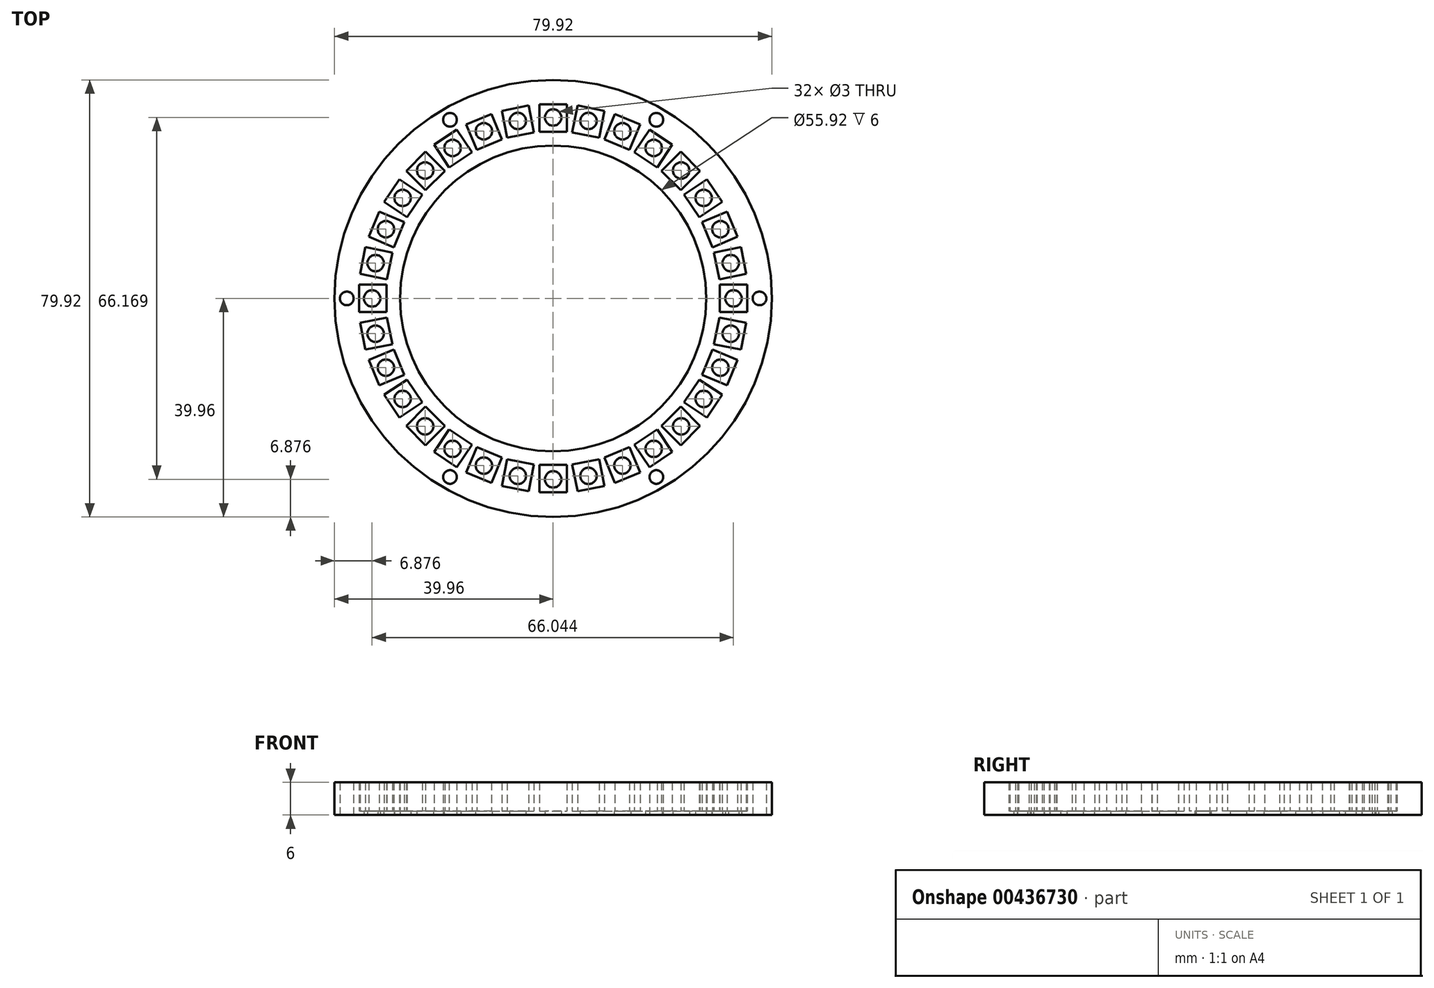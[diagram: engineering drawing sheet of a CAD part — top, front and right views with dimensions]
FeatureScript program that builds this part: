
annotation { "Feature Type Name" : "Feature", "Feature Type Description" : "" }
export const myFeature = defineFeature(function(context is Context, id is Id, definition is map)
    precondition{}
    {
        {
            var Q0;
            Q0=qCreatedBy(makeId("Top.planeOp"),FACE);
            var sketch = newSketch(context, id + "F0", { "sketchPlane" : qUnion([Q0])});
            skPoint(sketch, "E0.0.midPoint", {"position": v(30.46, 0) * mm});
            skLineSegment(sketch, "E1", {"start": v(0, 0) * mm, "end": v(46.47, 0) * mm, "construction": true});
            skLineSegment(sketch, "E2", {"start": v(30.46, 2.5) * mm, "end": v(35.46, 2.5) * mm, "construction": true});
            skLineSegment(sketch, "E3", {"start": v(35.46, 2.5) * mm, "end": v(35.46, -2.5) * mm, "construction": true});
            skLineSegment(sketch, "E4", {"start": v(35.46, -2.5) * mm, "end": v(30.46, -2.5) * mm, "construction": true});
            skCircle(sketch, "E5.cCircle", {"center": v(0, 0) * mm, "radius": 30.46 * mm, "construction": true});
            skLineSegment(sketch, "E5.0", {"start": v(30.46, 3) * mm, "end": v(30.46, -3) * mm});
            skLineSegment(sketch, "E5.1", {"start": v(30.46, -3) * mm, "end": v(29.29, -8.88) * mm});
            skLineSegment(sketch, "E5.2", {"start": v(29.29, -8.88) * mm, "end": v(27, -14.43) * mm});
            skLineSegment(sketch, "E5.3", {"start": v(27, -14.43) * mm, "end": v(23.66, -19.42) * mm});
            skLineSegment(sketch, "E5.4", {"start": v(23.66, -19.42) * mm, "end": v(19.42, -23.66) * mm});
            skLineSegment(sketch, "E5.5", {"start": v(19.42, -23.66) * mm, "end": v(14.43, -27) * mm});
            skLineSegment(sketch, "E5.6", {"start": v(14.43, -27) * mm, "end": v(8.88, -29.29) * mm});
            skLineSegment(sketch, "E5.7", {"start": v(8.88, -29.29) * mm, "end": v(3, -30.46) * mm});
            skLineSegment(sketch, "E5.8", {"start": v(3, -30.46) * mm, "end": v(-3, -30.46) * mm});
            skLineSegment(sketch, "E5.9", {"start": v(-3, -30.46) * mm, "end": v(-8.88, -29.29) * mm});
            skLineSegment(sketch, "E5.10", {"start": v(-8.88, -29.29) * mm, "end": v(-14.43, -27) * mm});
            skLineSegment(sketch, "E5.11", {"start": v(-14.43, -27) * mm, "end": v(-19.42, -23.66) * mm});
            skLineSegment(sketch, "E5.12", {"start": v(-19.42, -23.66) * mm, "end": v(-23.66, -19.42) * mm});
            skLineSegment(sketch, "E5.13", {"start": v(-23.66, -19.42) * mm, "end": v(-27, -14.43) * mm});
            skLineSegment(sketch, "E5.14", {"start": v(-27, -14.43) * mm, "end": v(-29.29, -8.88) * mm});
            skLineSegment(sketch, "E5.15", {"start": v(-29.29, -8.88) * mm, "end": v(-30.46, -3) * mm});
            skLineSegment(sketch, "E5.16", {"start": v(-30.46, -3) * mm, "end": v(-30.46, 3) * mm});
            skLineSegment(sketch, "E5.17", {"start": v(-30.46, 3) * mm, "end": v(-29.29, 8.88) * mm});
            skLineSegment(sketch, "E5.18", {"start": v(-29.29, 8.88) * mm, "end": v(-27, 14.43) * mm});
            skLineSegment(sketch, "E5.19", {"start": v(-27, 14.43) * mm, "end": v(-23.66, 19.42) * mm});
            skLineSegment(sketch, "E5.20", {"start": v(-23.66, 19.42) * mm, "end": v(-19.42, 23.66) * mm});
            skLineSegment(sketch, "E5.21", {"start": v(-19.42, 23.66) * mm, "end": v(-14.43, 27) * mm});
            skLineSegment(sketch, "E5.22", {"start": v(-14.43, 27) * mm, "end": v(-8.88, 29.29) * mm});
            skLineSegment(sketch, "E5.23", {"start": v(-8.88, 29.29) * mm, "end": v(-3, 30.46) * mm});
            skLineSegment(sketch, "E5.24", {"start": v(-3, 30.46) * mm, "end": v(3, 30.46) * mm});
            skLineSegment(sketch, "E5.25", {"start": v(3, 30.46) * mm, "end": v(8.88, 29.29) * mm});
            skLineSegment(sketch, "E5.26", {"start": v(8.88, 29.29) * mm, "end": v(14.43, 27) * mm});
            skLineSegment(sketch, "E5.27", {"start": v(14.43, 27) * mm, "end": v(19.42, 23.66) * mm});
            skLineSegment(sketch, "E5.28", {"start": v(19.42, 23.66) * mm, "end": v(23.66, 19.42) * mm});
            skLineSegment(sketch, "E5.29", {"start": v(23.66, 19.42) * mm, "end": v(27, 14.43) * mm});
            skLineSegment(sketch, "E5.30", {"start": v(27, 14.43) * mm, "end": v(29.29, 8.88) * mm});
            skLineSegment(sketch, "E5.31", {"start": v(29.29, 8.88) * mm, "end": v(30.46, 3) * mm});
            skPoint(sketch, "E6", {"position": v(35.46, 0) * mm});
            skSolve(sketch);
        }
        {
            var Q0;
            Q0=qCreatedBy(makeId("Top.planeOp"),FACE);
            cPlane(context, id + "F1", {"entities" : qUnion([Q0]), "cplaneType" : CPlaneType.OFFSET, "offset" : 0.75 * mm, "oppositeDirection" : true, "width" : 150 * mm, "height" : 150 * mm});
        }
        {
            var Q0;
            Q0=qCreatedBy(id+"F1.planeOp",FACE);
            var sketch = newSketch(context, id + "F2", { "sketchPlane" : qUnion([Q0])});
            skCircle(sketch, "E7", {"center": v(32.96, 0) * mm, "radius": 1.5 * mm});
            skCircle(sketch, "E8.1.0", {"center": v(32.45, -6.45) * mm, "radius": 1.5 * mm});
            skCircle(sketch, "E8.2.0", {"center": v(30.57, -12.66) * mm, "radius": 1.5 * mm});
            skCircle(sketch, "E8.3.0", {"center": v(27.5, -18.38) * mm, "radius": 1.5 * mm});
            skCircle(sketch, "E8.4.0", {"center": v(23.4, -23.4) * mm, "radius": 1.5 * mm});
            skCircle(sketch, "E8.5.0", {"center": v(18.38, -27.5) * mm, "radius": 1.5 * mm});
            skCircle(sketch, "E8.6.0", {"center": v(12.66, -30.57) * mm, "radius": 1.5 * mm});
            skCircle(sketch, "E8.7.0", {"center": v(6.45, -32.45) * mm, "radius": 1.5 * mm});
            skCircle(sketch, "E8.8.0", {"center": v(0, -33.08) * mm, "radius": 1.5 * mm});
            skCircle(sketch, "E8.9.0", {"center": v(-6.45, -32.45) * mm, "radius": 1.5 * mm});
            skCircle(sketch, "E8.10.0", {"center": v(-12.66, -30.57) * mm, "radius": 1.5 * mm});
            skCircle(sketch, "E8.11.0", {"center": v(-18.38, -27.5) * mm, "radius": 1.5 * mm});
            skCircle(sketch, "E8.12.0", {"center": v(-23.4, -23.4) * mm, "radius": 1.5 * mm});
            skCircle(sketch, "E8.13.0", {"center": v(-27.5, -18.38) * mm, "radius": 1.5 * mm});
            skCircle(sketch, "E8.14.0", {"center": v(-30.57, -12.66) * mm, "radius": 1.5 * mm});
            skCircle(sketch, "E8.15.0", {"center": v(-32.45, -6.45) * mm, "radius": 1.5 * mm});
            skLineSegment(sketch, "E8.anchor1", {"start": v(0, 0) * mm, "end": v(32.96, 0) * mm, "construction": true});
            skLineSegment(sketch, "E8.anchor2", {"start": v(0, 0) * mm, "end": v(32.45, 6.45) * mm, "construction": true});
            skLineSegment(sketch, "E9.2.1", {"start": v(22.46, 30.91) * mm, "end": v(22.46, 30.91) * mm});
            skPoint(sketch, "E9.center", {"position": v(0, 0) * mm});
            skCircle(sketch, "E10", {"center": v(0, 0) * mm, "radius": 27.96 * mm});
            skCircle(sketch, "E11.1.16.0", {"center": v(-33.08, 0) * mm, "radius": 1.5 * mm});
            skCircle(sketch, "E11.1.17.0", {"center": v(-32.45, 6.45) * mm, "radius": 1.5 * mm});
            skCircle(sketch, "E11.1.18.0", {"center": v(-30.57, 12.66) * mm, "radius": 1.5 * mm});
            skCircle(sketch, "E11.1.19.0", {"center": v(-27.5, 18.38) * mm, "radius": 1.5 * mm});
            skCircle(sketch, "E11.1.20.0", {"center": v(-23.4, 23.4) * mm, "radius": 1.5 * mm});
            skCircle(sketch, "E11.1.21.0", {"center": v(-18.38, 27.5) * mm, "radius": 1.5 * mm});
            skCircle(sketch, "E11.1.22.0", {"center": v(-12.66, 30.57) * mm, "radius": 1.5 * mm});
            skCircle(sketch, "E11.1.23.0", {"center": v(-6.45, 32.45) * mm, "radius": 1.5 * mm});
            skCircle(sketch, "E11.1.24.0", {"center": v(0, 33.08) * mm, "radius": 1.5 * mm});
            skCircle(sketch, "E11.1.25.0", {"center": v(6.45, 32.45) * mm, "radius": 1.5 * mm});
            skCircle(sketch, "E11.1.26.0", {"center": v(12.66, 30.57) * mm, "radius": 1.5 * mm});
            skCircle(sketch, "E11.1.27.0", {"center": v(18.38, 27.5) * mm, "radius": 1.5 * mm});
            skCircle(sketch, "E11.1.28.0", {"center": v(23.4, 23.4) * mm, "radius": 1.5 * mm});
            skCircle(sketch, "E11.1.29.0", {"center": v(27.5, 18.38) * mm, "radius": 1.5 * mm});
            skCircle(sketch, "E11.1.30.0", {"center": v(30.57, 12.66) * mm, "radius": 1.5 * mm});
            skCircle(sketch, "E11.1.31.0", {"center": v(32.45, 6.45) * mm, "radius": 1.5 * mm});
            skCircle(sketch, "E12", {"center": v(0, 0) * mm, "radius": 39.96 * mm});
            skCircle(sketch, "E13", {"center": v(37.7, 0) * mm, "radius": 1.25 * mm});
            skCircle(sketch, "E14.1.0", {"center": v(18.85, 32.66) * mm, "radius": 1.25 * mm});
            skCircle(sketch, "E14.2.0", {"center": v(-18.85, 32.66) * mm, "radius": 1.25 * mm});
            skCircle(sketch, "E14.3.0", {"center": v(-37.7, 0) * mm, "radius": 1.25 * mm});
            skCircle(sketch, "E14.4.0", {"center": v(-18.85, -32.66) * mm, "radius": 1.25 * mm});
            skCircle(sketch, "E14.5.0", {"center": v(18.85, -32.66) * mm, "radius": 1.25 * mm});
            skSolve(sketch);
        }
        {
            var Q0;
            Q0=qSketchRegion(id+"F2",true);
            extrude(context, id + "F3", {"entities" : qUnion([Q0]), "depth" : 6 * mm, "offsetDistance" : 25 * mm});
        }
        {
            var Q0;
            Q0=qCreatedBy(makeId("Top.planeOp"),FACE);
            var sketch = newSketch(context, id + "F4", { "sketchPlane" : qUnion([Q0])});
            skLineSegment(sketch, "E15.0", {"start": v(30.46, 2.5) * mm, "end": v(35.46, 2.5) * mm});
            skLineSegment(sketch, "E16.0", {"start": v(35.46, 2.5) * mm, "end": v(35.46, -2.5) * mm});
            skLineSegment(sketch, "E17.0", {"start": v(35.46, -2.5) * mm, "end": v(30.46, -2.5) * mm});
            skLineSegment(sketch, "E18", {"start": v(30.46, 2.5) * mm, "end": v(30.46, -2.5) * mm});
            skLineSegment(sketch, "E19.1.0", {"start": v(29.39, 8.4) * mm, "end": v(34.3, 9.37) * mm});
            skLineSegment(sketch, "E19.1.1", {"start": v(29.39, 8.4) * mm, "end": v(30.36, 3.5) * mm});
            skLineSegment(sketch, "E19.1.2", {"start": v(35.27, 4.47) * mm, "end": v(30.36, 3.5) * mm});
            skLineSegment(sketch, "E19.1.3", {"start": v(34.3, 9.37) * mm, "end": v(35.27, 4.47) * mm});
            skLineSegment(sketch, "E19.2.0", {"start": v(27.18, 13.97) * mm, "end": v(31.8, 15.88) * mm});
            skLineSegment(sketch, "E19.2.1", {"start": v(27.18, 13.97) * mm, "end": v(29.1, 9.35) * mm});
            skLineSegment(sketch, "E19.2.2", {"start": v(33.72, 11.26) * mm, "end": v(29.1, 9.35) * mm});
            skLineSegment(sketch, "E19.2.3", {"start": v(31.8, 15.88) * mm, "end": v(33.72, 11.26) * mm});
            skLineSegment(sketch, "E19.3.0", {"start": v(23.94, 19) * mm, "end": v(28.1, 21.78) * mm});
            skLineSegment(sketch, "E19.3.1", {"start": v(23.94, 19) * mm, "end": v(26.72, 14.84) * mm});
            skLineSegment(sketch, "E19.3.2", {"start": v(30.87, 17.62) * mm, "end": v(26.72, 14.84) * mm});
            skLineSegment(sketch, "E19.3.3", {"start": v(28.1, 21.78) * mm, "end": v(30.87, 17.62) * mm});
            skLineSegment(sketch, "E19.4.0", {"start": v(19.77, 23.3) * mm, "end": v(23.3, 26.84) * mm});
            skLineSegment(sketch, "E19.4.1", {"start": v(19.77, 23.3) * mm, "end": v(23.3, 19.77) * mm});
            skLineSegment(sketch, "E19.4.2", {"start": v(26.84, 23.3) * mm, "end": v(23.3, 19.77) * mm});
            skLineSegment(sketch, "E19.4.3", {"start": v(23.3, 26.84) * mm, "end": v(26.84, 23.3) * mm});
            skLineSegment(sketch, "E19.5.0", {"start": v(14.84, 26.72) * mm, "end": v(17.62, 30.87) * mm});
            skLineSegment(sketch, "E19.5.1", {"start": v(14.84, 26.72) * mm, "end": v(19, 23.94) * mm});
            skLineSegment(sketch, "E19.5.2", {"start": v(21.78, 28.1) * mm, "end": v(19, 23.94) * mm});
            skLineSegment(sketch, "E19.5.3", {"start": v(17.62, 30.87) * mm, "end": v(21.78, 28.1) * mm});
            skLineSegment(sketch, "E19.6.0", {"start": v(9.35, 29.1) * mm, "end": v(11.26, 33.72) * mm});
            skLineSegment(sketch, "E19.6.1", {"start": v(9.35, 29.1) * mm, "end": v(13.97, 27.18) * mm});
            skLineSegment(sketch, "E19.6.2", {"start": v(15.88, 31.8) * mm, "end": v(13.97, 27.18) * mm});
            skLineSegment(sketch, "E19.6.3", {"start": v(11.26, 33.72) * mm, "end": v(15.88, 31.8) * mm});
            skLineSegment(sketch, "E19.7.0", {"start": v(3.5, 30.36) * mm, "end": v(4.47, 35.27) * mm});
            skLineSegment(sketch, "E19.7.1", {"start": v(3.5, 30.36) * mm, "end": v(8.4, 29.39) * mm});
            skLineSegment(sketch, "E19.7.2", {"start": v(9.37, 34.3) * mm, "end": v(8.4, 29.39) * mm});
            skLineSegment(sketch, "E19.7.3", {"start": v(4.47, 35.27) * mm, "end": v(9.37, 34.3) * mm});
            skLineSegment(sketch, "E19.8.0", {"start": v(-2.5, 30.46) * mm, "end": v(-2.5, 35.46) * mm});
            skLineSegment(sketch, "E19.8.1", {"start": v(-2.5, 30.46) * mm, "end": v(2.5, 30.46) * mm});
            skLineSegment(sketch, "E19.8.2", {"start": v(2.5, 35.46) * mm, "end": v(2.5, 30.46) * mm});
            skLineSegment(sketch, "E19.8.3", {"start": v(-2.5, 35.46) * mm, "end": v(2.5, 35.46) * mm});
            skLineSegment(sketch, "E19.9.0", {"start": v(-8.4, 29.39) * mm, "end": v(-9.37, 34.3) * mm});
            skLineSegment(sketch, "E19.9.1", {"start": v(-8.4, 29.39) * mm, "end": v(-3.5, 30.36) * mm});
            skLineSegment(sketch, "E19.9.2", {"start": v(-4.47, 35.27) * mm, "end": v(-3.5, 30.36) * mm});
            skLineSegment(sketch, "E19.9.3", {"start": v(-9.37, 34.3) * mm, "end": v(-4.47, 35.27) * mm});
            skLineSegment(sketch, "E19.10.0", {"start": v(-13.97, 27.18) * mm, "end": v(-15.88, 31.8) * mm});
            skLineSegment(sketch, "E19.10.1", {"start": v(-13.97, 27.18) * mm, "end": v(-9.35, 29.1) * mm});
            skLineSegment(sketch, "E19.10.2", {"start": v(-11.26, 33.72) * mm, "end": v(-9.35, 29.1) * mm});
            skLineSegment(sketch, "E19.10.3", {"start": v(-15.88, 31.8) * mm, "end": v(-11.26, 33.72) * mm});
            skLineSegment(sketch, "E19.11.0", {"start": v(-19, 23.94) * mm, "end": v(-21.78, 28.1) * mm});
            skLineSegment(sketch, "E19.11.1", {"start": v(-19, 23.94) * mm, "end": v(-14.84, 26.72) * mm});
            skLineSegment(sketch, "E19.11.2", {"start": v(-17.62, 30.87) * mm, "end": v(-14.84, 26.72) * mm});
            skLineSegment(sketch, "E19.11.3", {"start": v(-21.78, 28.1) * mm, "end": v(-17.62, 30.87) * mm});
            skLineSegment(sketch, "E19.12.0", {"start": v(-23.3, 19.77) * mm, "end": v(-26.84, 23.3) * mm});
            skLineSegment(sketch, "E19.12.1", {"start": v(-23.3, 19.77) * mm, "end": v(-19.77, 23.3) * mm});
            skLineSegment(sketch, "E19.12.2", {"start": v(-23.3, 26.84) * mm, "end": v(-19.77, 23.3) * mm});
            skLineSegment(sketch, "E19.12.3", {"start": v(-26.84, 23.3) * mm, "end": v(-23.3, 26.84) * mm});
            skLineSegment(sketch, "E19.13.0", {"start": v(-26.72, 14.84) * mm, "end": v(-30.87, 17.62) * mm});
            skLineSegment(sketch, "E19.13.1", {"start": v(-26.72, 14.84) * mm, "end": v(-23.94, 19) * mm});
            skLineSegment(sketch, "E19.13.2", {"start": v(-28.1, 21.78) * mm, "end": v(-23.94, 19) * mm});
            skLineSegment(sketch, "E19.13.3", {"start": v(-30.87, 17.62) * mm, "end": v(-28.1, 21.78) * mm});
            skLineSegment(sketch, "E19.14.0", {"start": v(-29.1, 9.35) * mm, "end": v(-33.72, 11.26) * mm});
            skLineSegment(sketch, "E19.14.1", {"start": v(-29.1, 9.35) * mm, "end": v(-27.18, 13.97) * mm});
            skLineSegment(sketch, "E19.14.2", {"start": v(-31.8, 15.88) * mm, "end": v(-27.18, 13.97) * mm});
            skLineSegment(sketch, "E19.14.3", {"start": v(-33.72, 11.26) * mm, "end": v(-31.8, 15.88) * mm});
            skLineSegment(sketch, "E19.15.0", {"start": v(-30.36, 3.5) * mm, "end": v(-35.27, 4.47) * mm});
            skLineSegment(sketch, "E19.15.1", {"start": v(-30.36, 3.5) * mm, "end": v(-29.39, 8.4) * mm});
            skLineSegment(sketch, "E19.15.2", {"start": v(-34.3, 9.37) * mm, "end": v(-29.39, 8.4) * mm});
            skLineSegment(sketch, "E19.15.3", {"start": v(-35.27, 4.47) * mm, "end": v(-34.3, 9.37) * mm});
            skPoint(sketch, "E19.center", {"position": v(0, 0) * mm});
            skLineSegment(sketch, "E20.1.16.0", {"start": v(-30.46, -2.5) * mm, "end": v(-35.46, -2.5) * mm});
            skLineSegment(sketch, "E20.3.16.0", {"start": v(-30.46, -2.5) * mm, "end": v(-30.46, 2.5) * mm});
            skLineSegment(sketch, "E20.6.16.0", {"start": v(-35.46, 2.5) * mm, "end": v(-30.46, 2.5) * mm});
            skLineSegment(sketch, "E20.9.16.0", {"start": v(-35.46, -2.5) * mm, "end": v(-35.46, 2.5) * mm});
            skLineSegment(sketch, "E20.1.17.0", {"start": v(-29.39, -8.4) * mm, "end": v(-34.3, -9.37) * mm});
            skLineSegment(sketch, "E20.3.17.0", {"start": v(-29.39, -8.4) * mm, "end": v(-30.36, -3.5) * mm});
            skLineSegment(sketch, "E20.6.17.0", {"start": v(-35.27, -4.47) * mm, "end": v(-30.36, -3.5) * mm});
            skLineSegment(sketch, "E20.9.17.0", {"start": v(-34.3, -9.37) * mm, "end": v(-35.27, -4.47) * mm});
            skLineSegment(sketch, "E20.1.18.0", {"start": v(-27.18, -13.97) * mm, "end": v(-31.8, -15.88) * mm});
            skLineSegment(sketch, "E20.3.18.0", {"start": v(-27.18, -13.97) * mm, "end": v(-29.1, -9.35) * mm});
            skLineSegment(sketch, "E20.6.18.0", {"start": v(-33.72, -11.26) * mm, "end": v(-29.1, -9.35) * mm});
            skLineSegment(sketch, "E20.9.18.0", {"start": v(-31.8, -15.88) * mm, "end": v(-33.72, -11.26) * mm});
            skLineSegment(sketch, "E20.1.19.0", {"start": v(-23.94, -19) * mm, "end": v(-28.1, -21.78) * mm});
            skLineSegment(sketch, "E20.3.19.0", {"start": v(-23.94, -19) * mm, "end": v(-26.72, -14.84) * mm});
            skLineSegment(sketch, "E20.6.19.0", {"start": v(-30.87, -17.62) * mm, "end": v(-26.72, -14.84) * mm});
            skLineSegment(sketch, "E20.9.19.0", {"start": v(-28.1, -21.78) * mm, "end": v(-30.87, -17.62) * mm});
            skLineSegment(sketch, "E20.1.20.0", {"start": v(-19.77, -23.3) * mm, "end": v(-23.3, -26.84) * mm});
            skLineSegment(sketch, "E20.3.20.0", {"start": v(-19.77, -23.3) * mm, "end": v(-23.3, -19.77) * mm});
            skLineSegment(sketch, "E20.6.20.0", {"start": v(-26.84, -23.3) * mm, "end": v(-23.3, -19.77) * mm});
            skLineSegment(sketch, "E20.9.20.0", {"start": v(-23.3, -26.84) * mm, "end": v(-26.84, -23.3) * mm});
            skLineSegment(sketch, "E20.1.21.0", {"start": v(-14.84, -26.72) * mm, "end": v(-17.62, -30.87) * mm});
            skLineSegment(sketch, "E20.3.21.0", {"start": v(-14.84, -26.72) * mm, "end": v(-19, -23.94) * mm});
            skLineSegment(sketch, "E20.6.21.0", {"start": v(-21.78, -28.1) * mm, "end": v(-19, -23.94) * mm});
            skLineSegment(sketch, "E20.9.21.0", {"start": v(-17.62, -30.87) * mm, "end": v(-21.78, -28.1) * mm});
            skLineSegment(sketch, "E20.1.22.0", {"start": v(-9.35, -29.1) * mm, "end": v(-11.26, -33.72) * mm});
            skLineSegment(sketch, "E20.3.22.0", {"start": v(-9.35, -29.1) * mm, "end": v(-13.97, -27.18) * mm});
            skLineSegment(sketch, "E20.6.22.0", {"start": v(-15.88, -31.8) * mm, "end": v(-13.97, -27.18) * mm});
            skLineSegment(sketch, "E20.9.22.0", {"start": v(-11.26, -33.72) * mm, "end": v(-15.88, -31.8) * mm});
            skLineSegment(sketch, "E20.1.23.0", {"start": v(-3.5, -30.36) * mm, "end": v(-4.47, -35.27) * mm});
            skLineSegment(sketch, "E20.3.23.0", {"start": v(-3.5, -30.36) * mm, "end": v(-8.4, -29.39) * mm});
            skLineSegment(sketch, "E20.6.23.0", {"start": v(-9.37, -34.3) * mm, "end": v(-8.4, -29.39) * mm});
            skLineSegment(sketch, "E20.9.23.0", {"start": v(-4.47, -35.27) * mm, "end": v(-9.37, -34.3) * mm});
            skLineSegment(sketch, "E20.1.24.0", {"start": v(2.5, -30.46) * mm, "end": v(2.5, -35.46) * mm});
            skLineSegment(sketch, "E20.3.24.0", {"start": v(2.5, -30.46) * mm, "end": v(-2.5, -30.46) * mm});
            skLineSegment(sketch, "E20.6.24.0", {"start": v(-2.5, -35.46) * mm, "end": v(-2.5, -30.46) * mm});
            skLineSegment(sketch, "E20.9.24.0", {"start": v(2.5, -35.46) * mm, "end": v(-2.5, -35.46) * mm});
            skLineSegment(sketch, "E20.1.25.0", {"start": v(8.4, -29.39) * mm, "end": v(9.37, -34.3) * mm});
            skLineSegment(sketch, "E20.3.25.0", {"start": v(8.4, -29.39) * mm, "end": v(3.5, -30.36) * mm});
            skLineSegment(sketch, "E20.6.25.0", {"start": v(4.47, -35.27) * mm, "end": v(3.5, -30.36) * mm});
            skLineSegment(sketch, "E20.9.25.0", {"start": v(9.37, -34.3) * mm, "end": v(4.47, -35.27) * mm});
            skLineSegment(sketch, "E20.1.26.0", {"start": v(13.97, -27.18) * mm, "end": v(15.88, -31.8) * mm});
            skLineSegment(sketch, "E20.3.26.0", {"start": v(13.97, -27.18) * mm, "end": v(9.35, -29.1) * mm});
            skLineSegment(sketch, "E20.6.26.0", {"start": v(11.26, -33.72) * mm, "end": v(9.35, -29.1) * mm});
            skLineSegment(sketch, "E20.9.26.0", {"start": v(15.88, -31.8) * mm, "end": v(11.26, -33.72) * mm});
            skLineSegment(sketch, "E20.1.27.0", {"start": v(19, -23.94) * mm, "end": v(21.78, -28.1) * mm});
            skLineSegment(sketch, "E20.3.27.0", {"start": v(19, -23.94) * mm, "end": v(14.84, -26.72) * mm});
            skLineSegment(sketch, "E20.6.27.0", {"start": v(17.62, -30.87) * mm, "end": v(14.84, -26.72) * mm});
            skLineSegment(sketch, "E20.9.27.0", {"start": v(21.78, -28.1) * mm, "end": v(17.62, -30.87) * mm});
            skLineSegment(sketch, "E20.1.28.0", {"start": v(23.3, -19.77) * mm, "end": v(26.84, -23.3) * mm});
            skLineSegment(sketch, "E20.3.28.0", {"start": v(23.3, -19.77) * mm, "end": v(19.77, -23.3) * mm});
            skLineSegment(sketch, "E20.6.28.0", {"start": v(23.3, -26.84) * mm, "end": v(19.77, -23.3) * mm});
            skLineSegment(sketch, "E20.9.28.0", {"start": v(26.84, -23.3) * mm, "end": v(23.3, -26.84) * mm});
            skLineSegment(sketch, "E20.1.29.0", {"start": v(26.72, -14.84) * mm, "end": v(30.87, -17.62) * mm});
            skLineSegment(sketch, "E20.3.29.0", {"start": v(26.72, -14.84) * mm, "end": v(23.94, -19) * mm});
            skLineSegment(sketch, "E20.6.29.0", {"start": v(28.1, -21.78) * mm, "end": v(23.94, -19) * mm});
            skLineSegment(sketch, "E20.9.29.0", {"start": v(30.87, -17.62) * mm, "end": v(28.1, -21.78) * mm});
            skLineSegment(sketch, "E20.1.30.0", {"start": v(29.1, -9.35) * mm, "end": v(33.72, -11.26) * mm});
            skLineSegment(sketch, "E20.3.30.0", {"start": v(29.1, -9.35) * mm, "end": v(27.18, -13.97) * mm});
            skLineSegment(sketch, "E20.6.30.0", {"start": v(31.8, -15.88) * mm, "end": v(27.18, -13.97) * mm});
            skLineSegment(sketch, "E20.9.30.0", {"start": v(33.72, -11.26) * mm, "end": v(31.8, -15.88) * mm});
            skLineSegment(sketch, "E20.1.31.0", {"start": v(30.36, -3.5) * mm, "end": v(35.27, -4.47) * mm});
            skLineSegment(sketch, "E20.3.31.0", {"start": v(30.36, -3.5) * mm, "end": v(29.39, -8.4) * mm});
            skLineSegment(sketch, "E20.6.31.0", {"start": v(34.3, -9.37) * mm, "end": v(29.39, -8.4) * mm});
            skLineSegment(sketch, "E20.9.31.0", {"start": v(35.27, -4.47) * mm, "end": v(34.3, -9.37) * mm});
            skSolve(sketch);
        }
        {
            var Q0;
            Q0=qSketchRegion(id+"F4",true);
            extrude(context, id + "F5", {"entities" : qUnion([Q0]), "operationType" : NewBodyOperationType.REMOVE, "depth" : 6 * mm, "offsetDistance" : 25 * mm});
        }
    });
